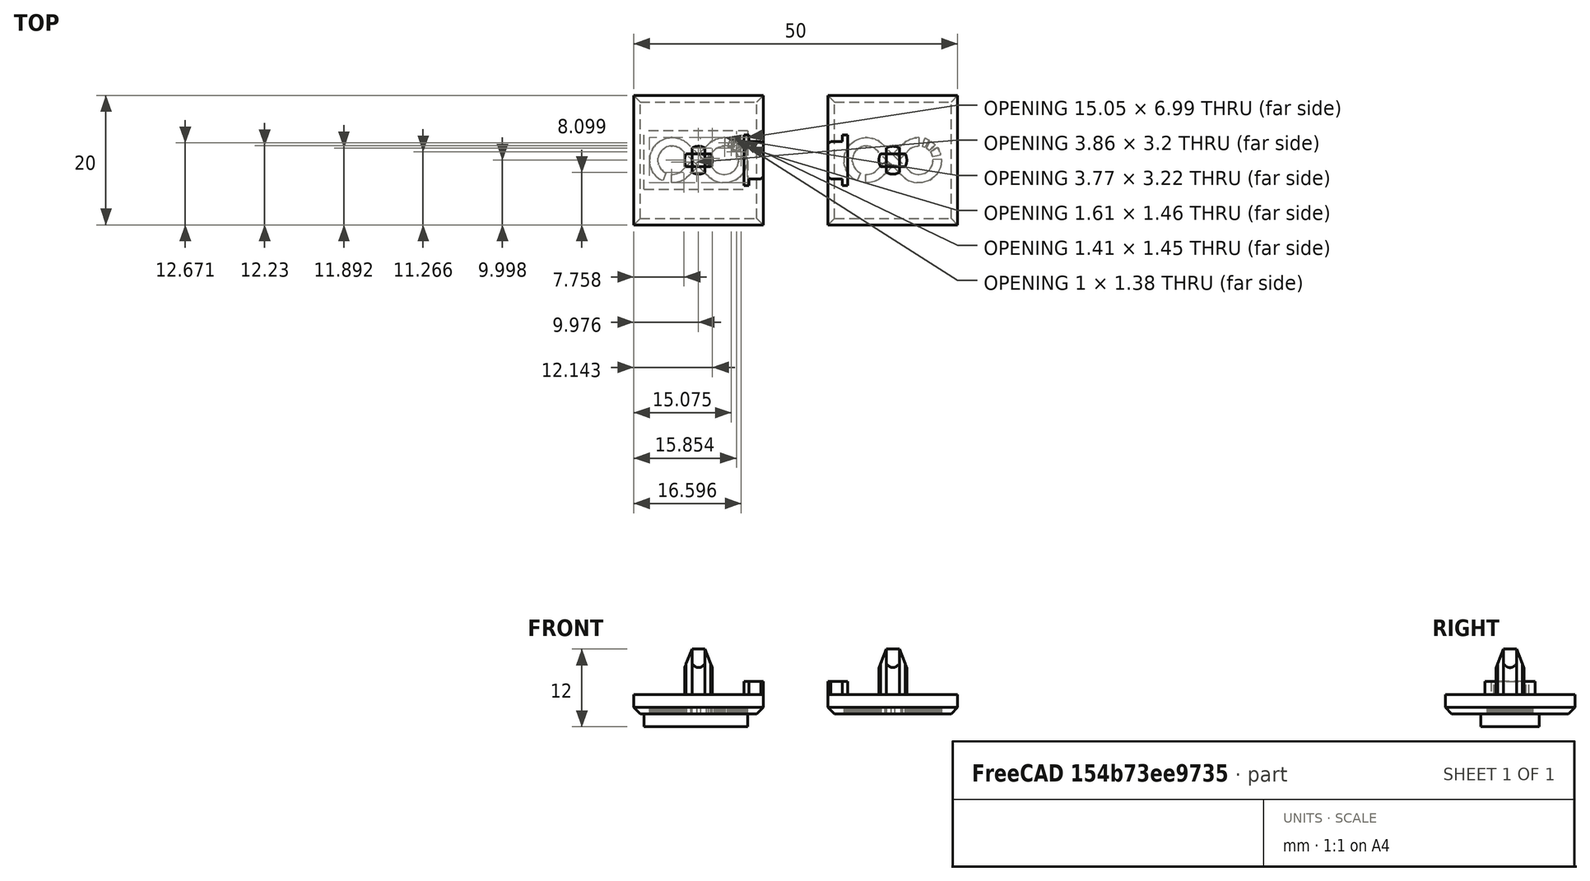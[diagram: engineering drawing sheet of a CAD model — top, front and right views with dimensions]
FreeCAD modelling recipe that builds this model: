
FCSTD DOCUMENT  (FreeCAD 0.19R24291 (Git))
Label: bed-end-cap
License: Other
LicenseURL: GPL3
objects: Part::Feature×5, Part::Box×3, Part::MultiFuse×3, Part::Chamfer×2, Part::Refine×1, Part::Mirroring×1, Part::Cut×1
note: 16 computed .brp shape members not serialized (recipe doc carries the construction recipe); baked Part::Feature solids carry a one-line shape summary decoded from their .brp

FEATURE [Part::Box] Box  label="Cube"
  AttacherType = Attacher::AttachEngine3D
  Height = 3
  Length = 20
  Placement = pos=(-10,-10,0) rot=(0,0,1;0rad)
  Width = 20
FEATURE [Part::Box] Box003  label="Cube003"
  AttacherType = Attacher::AttachEngine3D
  Height = 3
  Length = 3
  Placement = pos=(7,-2.9,2) rot=(0,0,1;0rad)
  Width = 5.8
FEATURE [Part::Box] Box004  label="Cube004"
  AttacherType = Attacher::AttachEngine3D
  Height = 3
  Length = 0.8
  Placement = pos=(7,-3.9,2) rot=(0,0,1;0rad)
  Width = 7.8
FEATURE [Part::Chamfer] Chamfer003
  Base = -> Box003
  Edges = 2 edges r=0.4: [Edge5,Edge7]
FEATURE [Part::MultiFuse] Fusion001  label="aligner"
  Shapes = -> [Chamfer003,Box004]
FEATURE [Part::Feature] Common001  label="axis-origib"
  shape: bbox 4.3 x 4.3 x 8 mm, 23 faces (baked)
FEATURE [Part::Feature] Part__Mirroring001  label="logo"
  Placement = pos=(10.4,-10.5,1) rot=(0,0,1;0rad)
  shape: bbox 16 x 9 x 3 mm, 304 faces (baked)
FEATURE [Part::Refine] Fusion001001  label="aligner001"
  Placement = pos=(30,-4e-15,0) rot=(0,0,1;3.14159rad)
  Source = -> Fusion001
FEATURE [Part::Feature] Common002  label="axis-origib001"
  Placement = pos=(30,0,0) rot=(0,0,1;0rad)
  shape: bbox 4.3 x 4.3 x 8 mm, 23 faces (baked)
FEATURE [Part::Mirroring] Part__Mirroring  label="logo (Mirror #1)"
  Base = (0,0,0)
  Normal = (1,0,0)
  Source = -> Part__Mirroring001
FEATURE [Part::Feature] Part__Mirroring002  label="logo (Mirror #1)001"
  shape: bbox 16 x 9 x 3 mm, 304 faces (baked)
FEATURE [Part::Cut] Cut
  Base = -> Box
  Tool = -> Part__Mirroring002
FEATURE [Part::Chamfer] Chamfer
  Base = -> Cut
  Edges = 4 edges r=1: [Edge4,Edge5,Edge10,Edge12]
FEATURE [Part::Feature] Chamfer004
  Placement = pos=(30,0,0) rot=(0,0,1;0rad)
  shape: bbox 20 x 20 x 3 mm, 309 faces (baked)
FEATURE [Part::MultiFuse] Fusion
  Shapes = -> [Chamfer,Common001,Fusion001]
FEATURE [Part::MultiFuse] Fusion001002
  Shapes = -> [Fusion001001,Chamfer004,Common002]
